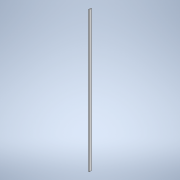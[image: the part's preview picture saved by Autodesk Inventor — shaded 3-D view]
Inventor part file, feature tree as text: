
AUTODESK INVENTOR PART (.ipt)
format: ipt  version: 2021 (Build 250183000, 183)  size: 93,696 bytes
history: native  units: mm
features: extrude x1, sketch x1
ambient origin geometry x8: Origin, YZ Plane, XZ Plane, XY Plane, X Axis, Y Axis, Z Axis, Center Point
bodies: Solid1 (feature_tree)
feature tree (2):
  extrude  "Extrusion1"  Depth=30.0mm
  sketch  "Sketch1"  dims[d0=10.0mm d1=30.0mm d2=1785.5mm d3=0.0mm]
